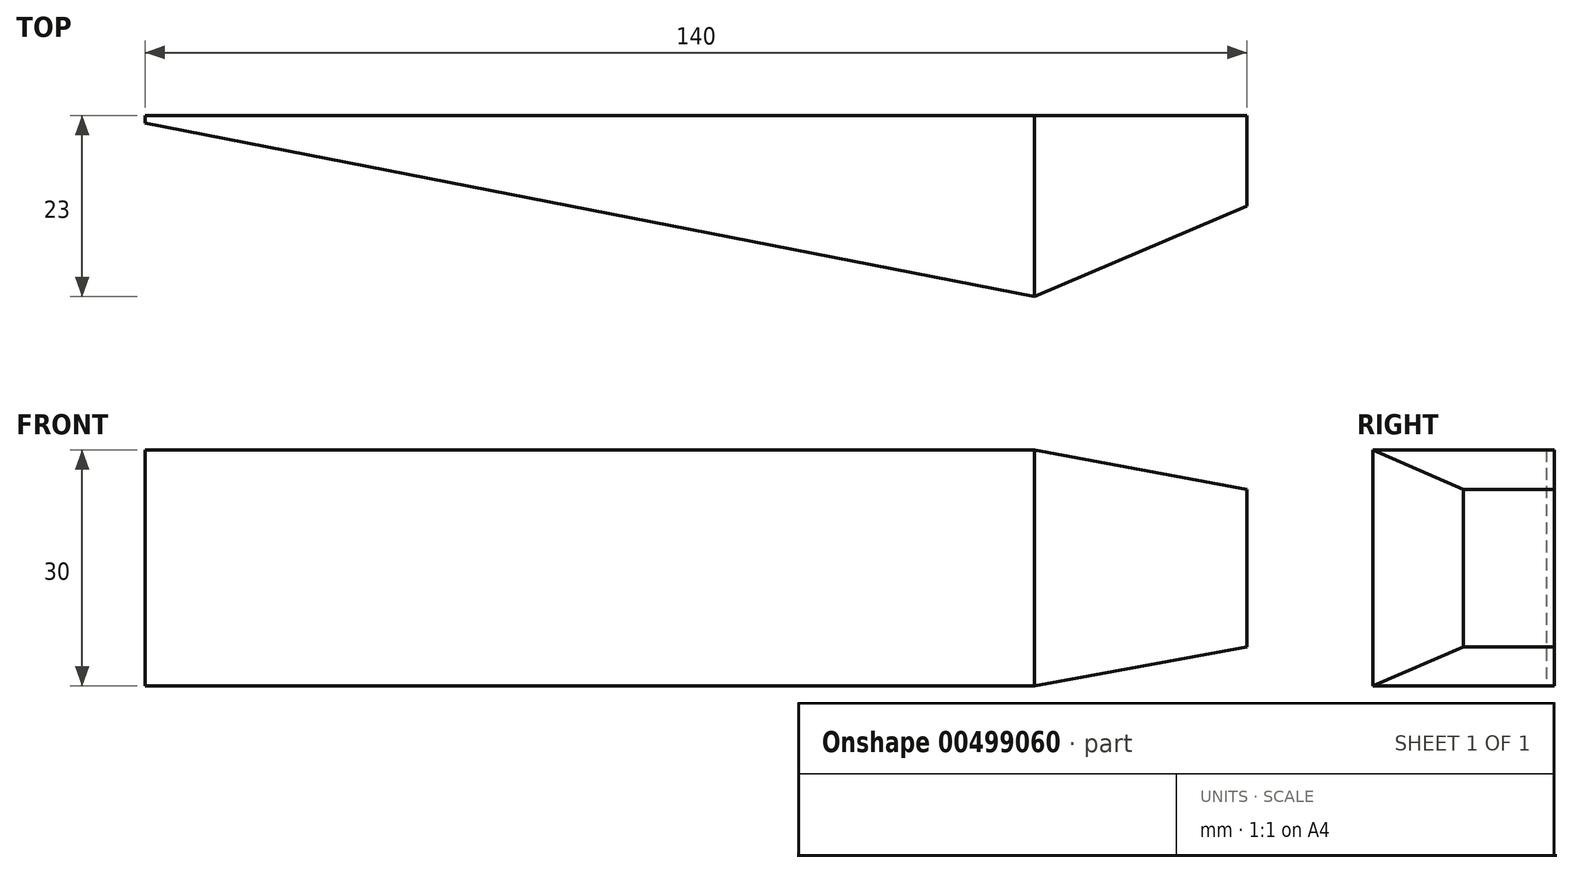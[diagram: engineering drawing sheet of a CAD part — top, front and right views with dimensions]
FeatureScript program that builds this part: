
annotation { "Feature Type Name" : "Feature", "Feature Type Description" : "" }
export const myFeature = defineFeature(function(context is Context, id is Id, definition is map)
    precondition{}
    {
        {
            var Q0;
            Q0=qCreatedBy(makeId("Top.planeOp"),FACE);
            var sketch = newSketch(context, id + "F0", { "sketchPlane" : qUnion([Q0])});
            skLineSegment(sketch, "E0", {"start": v(53.96, -374.41) * mm, "end": v(53.96, -385.91) * mm});
            skLineSegment(sketch, "E1", {"start": v(53.96, -385.91) * mm, "end": v(198.96, -385.91) * mm});
            skLineSegment(sketch, "E2", {"start": v(198.96, -385.91) * mm, "end": v(193.96, -385.91) * mm, "construction": true});
            skLineSegment(sketch, "E3", {"start": v(80.96, -362.91) * mm, "end": v(198.96, -385.91) * mm});
            skLineSegment(sketch, "E4", {"start": v(193.96, -385.91) * mm, "end": v(193.96, -384.94) * mm, "construction": true});
            skLineSegment(sketch, "E5", {"start": v(84.27, -363.56) * mm, "end": v(84.84, -360.61) * mm, "construction": true});
            skLineSegment(sketch, "E6", {"start": v(195.7, -385.28) * mm, "end": v(196.28, -382.33) * mm, "construction": true});
            skLineSegment(sketch, "E7", {"start": v(84.84, -360.61) * mm, "end": v(218.03, -386.57) * mm, "construction": true});
            skLineSegment(sketch, "E8", {"start": v(214.64, -385.91) * mm, "end": v(241.64, -385.91) * mm});
            skLineSegment(sketch, "E9", {"start": v(241.64, -385.91) * mm, "end": v(241.64, -362.91) * mm});
            skLineSegment(sketch, "E10", {"start": v(241.64, -362.91) * mm, "end": v(96.64, -362.91) * mm});
            skLineSegment(sketch, "E11", {"start": v(96.64, -362.91) * mm, "end": v(214.64, -385.91) * mm});
            skLineSegment(sketch, "E12", {"start": v(80.96, -362.91) * mm, "end": v(53.96, -374.41) * mm});
            skPoint(sketch, "E13.start.orphan", {"position": v(53.96, -362.91) * mm});
            skLineSegment(sketch, "E14", {"start": v(5, 0) * mm, "end": v(145, 0) * mm});
            skLineSegment(sketch, "E15", {"start": v(145, 0) * mm, "end": v(145, -11.5) * mm});
            skLineSegment(sketch, "E16", {"start": v(118, -23) * mm, "end": v(5, -0.97) * mm});
            skLineSegment(sketch, "E17", {"start": v(5, 0) * mm, "end": v(5, -0.97) * mm, "construction": true});
            skLineSegment(sketch, "E18", {"start": v(5, 0) * mm, "end": v(5, -0.97) * mm});
            skLineSegment(sketch, "E19", {"start": v(118, -23) * mm, "end": v(145, -11.5) * mm});
            skPoint(sketch, "E20.orphan", {"position": v(145, -23) * mm});
            skLineSegment(sketch, "E21", {"start": v(164.84, -274.28) * mm, "end": v(159.84, -274.28) * mm, "construction": true});
            skLineSegment(sketch, "E22", {"start": v(159.84, -274.28) * mm, "end": v(159.84, -273.3) * mm, "construction": true});
            skLineSegment(sketch, "E23", {"start": v(50.15, -251.92) * mm, "end": v(50.72, -248.98) * mm, "construction": true});
            skLineSegment(sketch, "E24", {"start": v(161.55, -271.28) * mm, "end": v(162.12, -268.33) * mm, "construction": true});
            skLineSegment(sketch, "E25", {"start": v(50.72, -248.98) * mm, "end": v(183.9, -274.94) * mm, "construction": true});
            skLineSegment(sketch, "E26", {"start": v(180.52, -274.28) * mm, "end": v(207.52, -274.28) * mm});
            skLineSegment(sketch, "E27", {"start": v(207.52, -274.28) * mm, "end": v(207.52, -251.28) * mm});
            skLineSegment(sketch, "E28", {"start": v(207.52, -251.28) * mm, "end": v(62.52, -251.28) * mm});
            skLineSegment(sketch, "E29", {"start": v(62.52, -251.28) * mm, "end": v(180.52, -274.28) * mm});
            skLineSegment(sketch, "E30", {"start": v(207.52, -251.28) * mm, "end": v(207.52, -271.28) * mm, "construction": true});
            skLineSegment(sketch, "E31", {"start": v(207.52, -271.28) * mm, "end": v(117.64, -271.28) * mm, "construction": true});
            skLineSegment(sketch, "E32", {"start": v(62.52, -251.28) * mm, "end": v(67.52, -251.28) * mm, "construction": true});
            skLineSegment(sketch, "E33", {"start": v(67.52, -251.28) * mm, "end": v(67.52, -252.25) * mm, "construction": true});
            skLineSegment(sketch, "E34", {"start": v(67.52, -252.25) * mm, "end": v(165.13, -271.28) * mm, "construction": true});
            skLineSegment(sketch, "E35", {"start": v(67.52, -252.25) * mm, "end": v(173.53, -272.91) * mm, "construction": true});
            skLineSegment(sketch, "E36", {"start": v(173.53, -272.91) * mm, "end": v(207.52, -272.91) * mm, "construction": true});
            skLineSegment(sketch, "E37", {"start": v(207.52, -272.91) * mm, "end": v(207.52, -251.28) * mm, "construction": true});
            skLineSegment(sketch, "E38", {"start": v(278.47, -100.18) * mm, "end": v(383.47, -120.65) * mm, "construction": true});
            skLineSegment(sketch, "E39", {"start": v(418.47, -110.7) * mm, "end": v(418.47, -99.2) * mm});
            skLineSegment(sketch, "E40", {"start": v(418.47, -99.2) * mm, "end": v(278.47, -99.2) * mm});
            skLineSegment(sketch, "E41", {"start": v(278.47, -100.18) * mm, "end": v(383.47, -120.65) * mm});
            skLineSegment(sketch, "E42", {"start": v(418.47, -99.2) * mm, "end": v(278.47, -99.2) * mm, "construction": true});
            skLineSegment(sketch, "E43", {"start": v(278.47, -99.2) * mm, "end": v(278.47, -100.18) * mm});
            skLineSegment(sketch, "E44", {"start": v(278.47, -99.2) * mm, "end": v(383.47, -99.2) * mm, "construction": true});
            skLineSegment(sketch, "E45", {"start": v(383.47, -99.2) * mm, "end": v(383.47, -120.65) * mm, "construction": true});
            skLineSegment(sketch, "E46", {"start": v(383.47, -120.65) * mm, "end": v(418.47, -110.7) * mm});
            skPoint(sketch, "E47.end.orphan", {"position": v(418.47, -120.65) * mm});
            skPoint(sketch, "E48.orphan", {"position": v(418.47, -122.2) * mm});
            skSolve(sketch);
        }
        {
            var Q0;
            Q0=makeQuery(id+"F0.imprint","IMPRINT",FACE,{"disambiguationData":[TD([[makeQuery(id+"F0.imprint","IMPRINT",EDGE,{"derivedFrom":sQuery(id+"F0.wireOp",EDGE,"E14")}),-1.0]])]});
            extrude(context, id + "F1", {"entities" : qUnion([Q0]), "depth" : 30 * mm});
        }
        {
            var Q0;
            Q0=qCreatedBy(makeId("Front.planeOp"),FACE);
            var sketch = newSketch(context, id + "F2", { "sketchPlane" : qUnion([Q0])});
            skLineSegment(sketch, "E49", {"start": v(0, 0) * mm, "end": v(145, 0) * mm, "construction": true});
            skLineSegment(sketch, "E50", {"start": v(145, 0) * mm, "end": v(118, 0) * mm});
            skLineSegment(sketch, "E51", {"start": v(145, 0) * mm, "end": v(145, 5) * mm});
            skLineSegment(sketch, "E52", {"start": v(145, 5) * mm, "end": v(145, 25) * mm, "construction": true});
            skLineSegment(sketch, "E53", {"start": v(145, 25) * mm, "end": v(145, 30) * mm, "construction": true});
            skLineSegment(sketch, "E54", {"start": v(118, 0) * mm, "end": v(118, 30) * mm, "construction": true});
            skLineSegment(sketch, "E55", {"start": v(118, 30) * mm, "end": v(145, 25) * mm});
            skLineSegment(sketch, "E56", {"start": v(118, 30) * mm, "end": v(145, 30) * mm});
            skLineSegment(sketch, "E57", {"start": v(145, 30) * mm, "end": v(145, 25) * mm});
            skLineSegment(sketch, "E58", {"start": v(145, 5) * mm, "end": v(118, 0) * mm});
            skLineSegment(sketch, "E59", {"start": v(118, 0) * mm, "end": v(145, 0) * mm});
            skSolve(sketch);
        }
        {
            var Q0;
            Q0 = qSketchRegion(id + "F2", true);
            extrude(context, id + "F3", {"entities" : qUnion([Q0]), "operationType" : NewBodyOperationType.REMOVE, "depth" : 25 * mm});
        }
    });
